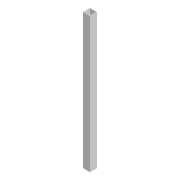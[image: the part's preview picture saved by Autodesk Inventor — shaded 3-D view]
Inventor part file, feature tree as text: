
AUTODESK INVENTOR PART (.ipt)
format: ipt  version: 2022 (Build 260153000, 153)  size: 82,432 bytes
history: native  units: mm
features: extrude x1, sketch x1
ambient origin geometry x8: Origin, YZ Plane, XZ Plane, XY Plane, X Axis, Y Axis, Z Axis, Center Point
bodies: Solid1 (feature_tree)
feature tree (2):
  extrude  "Extrusion1"  Depth=20.0mm
  sketch  "Sketch1"  dims[d0=20.0mm d1=20.0mm d2=1.0mm d3=383.0mm d4=0.0mm]
